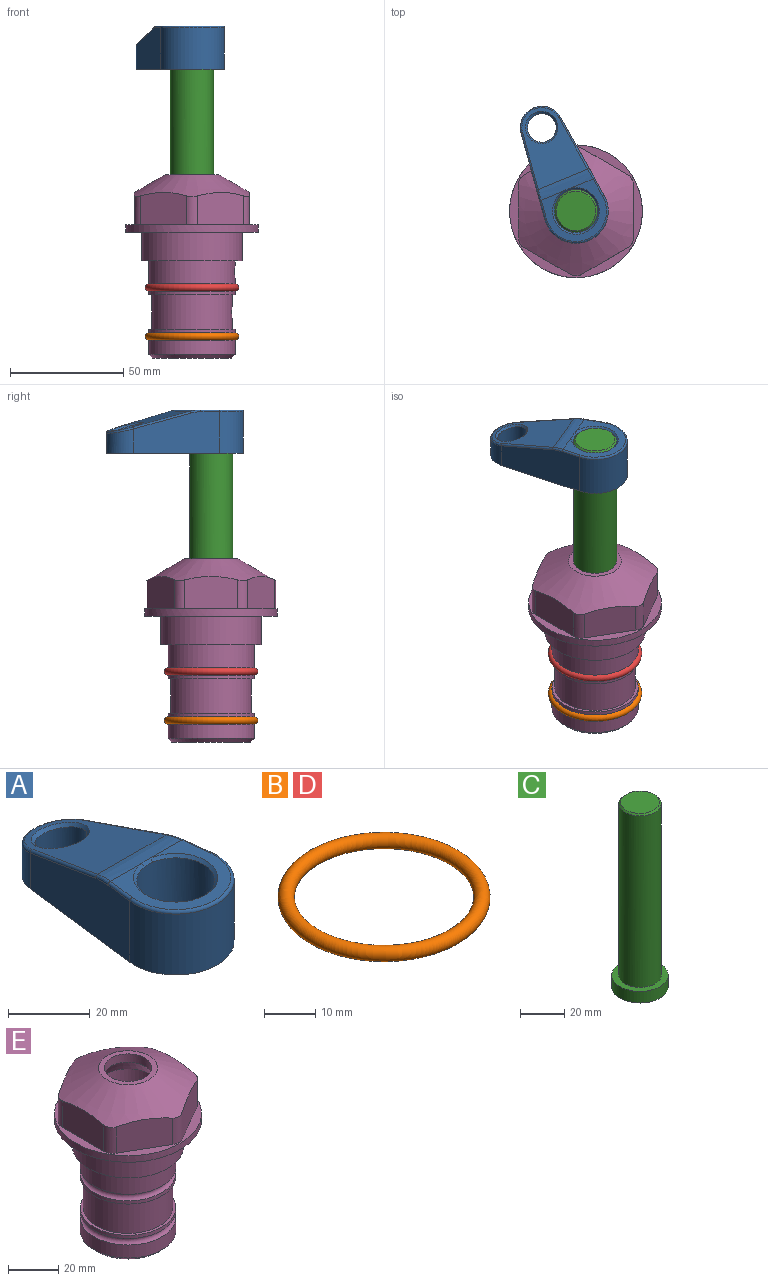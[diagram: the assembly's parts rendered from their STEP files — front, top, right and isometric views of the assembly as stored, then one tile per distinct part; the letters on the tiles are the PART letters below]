
ASSEMBLY  parts=5 mates=4
PART A: 31 faces, bbox 31.7x65.5x19.8 mm
  f0: plane 39.12x18.26mm, normal (0.99,0.12,0), area 612.2mm2, adj f1,f4,f7,f11,f13,f15
  f1: cylinder r=9.53mm len=18.91mm, axis (0,0,-1), area 296.1mm2, adj f0,f2,f7,f17
  f2: plane 39.12x18.26mm, normal (-0.99,0.12,0), area 612.2mm2, adj f1,f4,f7,f12,f14,f16
  f3: cylinder r=6.35mm len=12.7mm, axis (0,0,-1), area 362.4mm2, adj f7,f18
  f4: cylinder r=14.29mm len=28.58mm, axis (0,0,-1), area 882.2mm2, adj f0,f2,f7,f10
  f5: cylinder r=9.53mm len=19.05mm, axis (0,0,-1), area 1092.6mm2, adj f7,f19,f20
  f6: plane 26.99x23.69mm, normal (0,0,1), area 216.2mm2, adj f9,f10,f11,f12,f19
  f7: plane 63.5x28.58mm, normal (0,0,-1), area 661.8mm2, adj f0,f1,f2,f3,f4,f5,f22,f23
  f8: plane 33.52x23.6mm, normal (0,0.26,0.97), area 486mm2, adj f9,f15,f16,f17,f18
  f9: cylinder r=19.05mm len=24.72mm, axis (1,0,0), area 120.4mm2, adj f6,f8,f13,f14,f20
  f10: torus R=13.49mm, axis (0,0,1), area 59mm2, adj f4,f6,f11,f12
  f11: cylinder r=0.79mm len=8.67mm, axis (0.12,-0.99,0), area 10.8mm2, adj f0,f6,f10,f13
  f12: cylinder r=0.79mm len=8.67mm, axis (0.12,0.99,0), area 10.8mm2, adj f2,f6,f10,f14
  f13: bspline ~4.95x1.42mm, area 6.1mm2, adj f0,f9,f11,f15
  f14: bspline ~4.95x1.42mm, area 6.1mm2, adj f2,f9,f12,f16
  f15: cylinder r=0.79mm len=25.95mm, axis (0.12,-0.96,0.26), area 32.9mm2, adj f0,f8,f13,f17
  f16: cylinder r=0.79mm len=25.95mm, axis (0.12,0.96,-0.26), area 32.9mm2, adj f2,f8,f14,f17
  f17: bspline ~18.91x8.38mm, area 30mm2, adj f1,f8,f15,f16
  f18: bspline ~14.29x14.29mm, area 48.3mm2, adj f3,f8
  f19: cone r=9.53mm half-angle=45deg, axis (0,0,1), area 66.5mm2, adj f5,f6,f20
  f20: bspline ~3.22x0.96mm, area 3.5mm2, adj f5,f9,f19
  f21: plane 2.75x2.72mm, normal (0,0,-1), area 2.9mm2, adj f23,f25,f28
  f22: plane 23.05x15.88mm, normal (-0.99,-0.12,0), area 323.6mm2, adj f7,f25,f26,f27,f28,f29
  f23: plane 23.05x15.88mm, normal (0.99,-0.12,0), area 323.6mm2, adj f7,f21,f25,f27,f28,f30
  f24: cylinder r=9.53mm len=10.69mm, axis (0,0,-1), area 114.7mm2, adj f7,f27,f29,f30
  f25: cylinder r=12.7mm len=20.59mm, axis (0,0,-1), area 381.1mm2, adj f7,f21,f22,f23,f26,f28
  f26: plane 2.75x2.72mm, normal (0,0,-1), area 2.9mm2, adj f22,f25,f28
  f27: plane 19.72x18.37mm, normal (0,-0.26,-0.97), area 291.8mm2, adj f22,f23,f24,f28,f29,f30
  f28: cylinder r=15.88mm len=19.92mm, axis (1,0,0), area 54.8mm2, adj f21,f22,f23,f25,f26,f27
  f29: cylinder r=1.59mm len=11mm, axis (0,0,-1), area 34.7mm2, adj f7,f22,f24,f27
  f30: cylinder r=1.59mm len=11mm, axis (0,0,-1), area 34.7mm2, adj f7,f23,f24,f27
PART B: 1 faces, bbox 44.7x44.7x3.2 mm
  f0: torus R=19.05mm, axis (0,0,1), area 1193.9mm2
PART C: 6 faces, bbox 25.4x25.4x101.6 mm
  f0: plane 17.46x17.46mm, normal (0,0,1), area 239.5mm2, adj f5
  f1: plane 25.4x25.4mm, normal (0,0,-1), area 506.7mm2, adj f2
  f2: cylinder r=12.7mm len=25.4mm, axis (0,0,1), area 506.7mm2, adj f1,f3
  f3: plane 25.4x25.4mm, normal (0,0,1), area 221.7mm2, adj f2,f4
  f4: cylinder r=9.53mm len=94.46mm, axis (0,0,1), area 5653mm2, adj f3,f5
  f5: cone r=8.73mm half-angle=45deg, axis (0,0,-1), area 64.4mm2, adj f0,f4
PART D: same geometry as B
PART E: 36 faces, bbox 58.7x58.7x81 mm
  f0: cylinder r=17.78mm len=35.56mm, axis (0,0,1), area 1670.8mm2, adj f23,f24,f31
  f1: cylinder r=19.05mm len=38.1mm, axis (0,0,1), area 1191.9mm2, adj f26,f27,f30
  f2: plane 58.66x58.66mm, normal (0,0,-1), area 1150.6mm2, adj f3,f28
  f3: cylinder r=29.33mm len=58.66mm, axis (0,0,-1), area 585.1mm2, adj f2,f4
  f4: plane 58.66x58.66mm, normal (0,0,1), area 475.9mm2, adj f3,f5,f6,f7,f8,f9,f10,f11
  f5: plane 20.32x14.34mm, normal (-0.5,0.87,0), area 324.4mm2, adj f4,f15,f16,f17
  f6: plane 20.32x14.34mm, normal (0.5,0.87,0), area 324.4mm2, adj f4,f14,f15,f17
  f7: plane 23.48x14.34mm, normal (1,0,0), area 324.4mm2, adj f4,f13,f14,f17
  f8: plane 20.32x14.34mm, normal (0.5,-0.87,0), area 324.4mm2, adj f4,f12,f13,f17
  f9: plane 20.32x14.34mm, normal (-0.5,-0.87,0), area 324.4mm2, adj f4,f11,f12,f17
  f10: plane 23.48x14.34mm, normal (-1,0,0), area 324.4mm2, adj f4,f11,f16,f17
  f11: cylinder r=5.08mm len=12.85mm, axis (0,0,-1), area 67.2mm2, adj f4,f9,f10,f17
  f12: cylinder r=5.08mm len=12.85mm, axis (0,0,-1), area 67.2mm2, adj f4,f8,f9,f17
  f13: cylinder r=5.08mm len=12.85mm, axis (0,0,-1), area 67.2mm2, adj f4,f7,f8,f17
  f14: cylinder r=5.08mm len=12.85mm, axis (0,0,-1), area 67.2mm2, adj f4,f6,f7,f17
  f15: cylinder r=5.08mm len=12.85mm, axis (0,0,-1), area 67.2mm2, adj f4,f5,f6,f17
  f16: cylinder r=5.08mm len=12.85mm, axis (0,0,-1), area 67.2mm2, adj f4,f5,f10,f17
  f17: cone r=11.73mm half-angle=60deg, axis (0,0,-1), area 2071.8mm2, adj f5,f6,f7,f8,f9,f10,f11,f12
  f18: plane 23.46x23.46mm, normal (0,0,1), area 147.4mm2, adj f17,f35
  f19: plane 34.93x34.93mm, normal (0,0,-1), area 958mm2, adj f29
  f20: cylinder r=19.05mm len=38.1mm, axis (0,0,1), area 760.1mm2, adj f21,f29
  f21: torus R=19.05mm, axis (0,0,1), area 565.3mm2, adj f20,f22
  f22: cylinder r=19.05mm len=38.1mm, axis (0,0,1), area 190mm2, adj f21,f23
  f23: plane 38.1x38.1mm, normal (0,0,1), area 146.9mm2, adj f0,f22
  f24: plane 38.1x38.1mm, normal (0,0,-1), area 146.9mm2, adj f0,f25
  f25: cylinder r=19.05mm len=38.1mm, axis (0,0,1), area 190mm2, adj f24,f26
  f26: torus R=19.05mm, axis (0,0,1), area 565.3mm2, adj f1,f25
  f27: plane 44.45x44.45mm, normal (0,0,-1), area 411.7mm2, adj f1,f28
  f28: cylinder r=22.23mm len=44.45mm, axis (0,0,1), area 1773.5mm2, adj f2,f27
  f29: cone r=19.05mm half-angle=45deg, axis (0,0,1), area 257.5mm2, adj f19,f20
  f30: cylinder r=3.17mm len=6.75mm, axis (-1,0,0), area 128mm2, adj f1,f33
  f31: cylinder r=3.17mm len=6.35mm, axis (-1,0,0), area 102.5mm2, adj f0,f33
  f32: plane 25.4x25.4mm, normal (0,0,1), area 506.7mm2, adj f33
  f33: cylinder r=12.7mm len=66.42mm, axis (0,0,-1), area 5236.2mm2, adj f30,f31,f32,f34
  f34: cone r=9.53mm half-angle=30deg, axis (0,0,-1), area 443.4mm2, adj f33,f35
  f35: cylinder r=9.53mm len=19.05mm, axis (0,0,-1), area 240.9mm2, adj f18,f34
PLACE A rot(axis=(0,0,1),22.3deg) t=(0,0,27.55)mm
PLACE B t=(0,0,-21.59)mm
PLACE C rot(axis=(0,0,1),22.3deg) t=(0,0,27.55)mm
PLACE D at identity
PLACE E at identity fixed
MATE fastened D.f0 <-> E.f0  axis (0,0,1) through (0,0,-24.51)mm
MATE fastened C.f2 <-> A.f4  axis (0,0,1) through (0,0,91.05)mm
MATE cylindrical E.f0 <-> C.f2  axis (0,0,1) through (0,0,-50.55)mm
MATE fastened B.f0 <-> E.f0  axis (0,0,1) through (0,0,-46.1)mm
